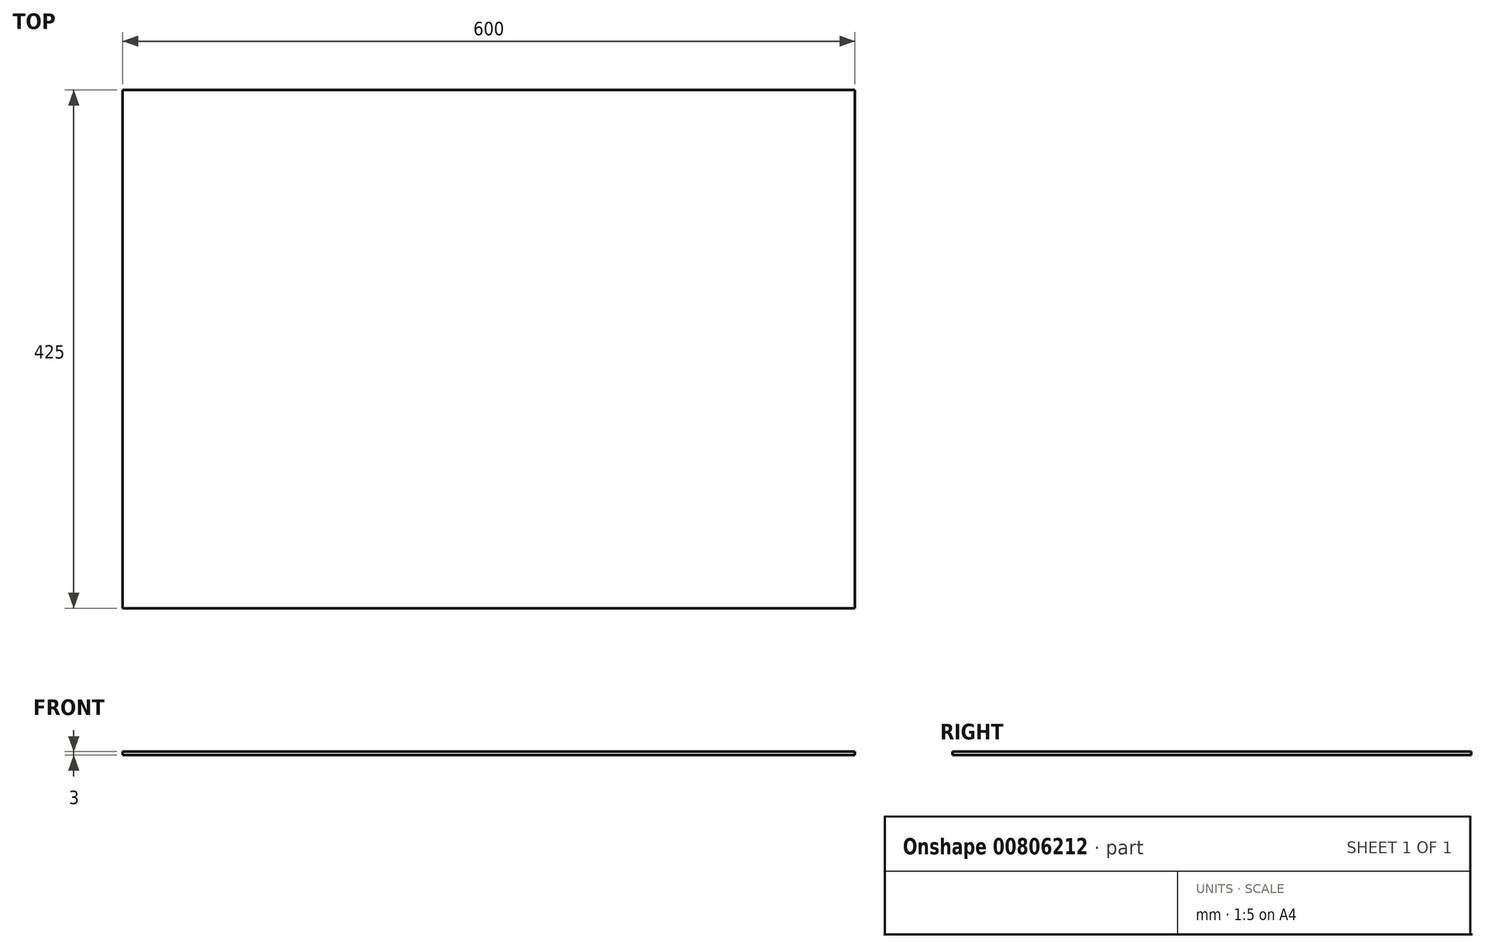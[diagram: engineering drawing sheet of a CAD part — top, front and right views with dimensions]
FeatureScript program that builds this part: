
annotation { "Feature Type Name" : "Feature", "Feature Type Description" : "" }
export const myFeature = defineFeature(function(context is Context, id is Id, definition is map)
    precondition{}
    {
        {
            var Q0;
            Q0=qCreatedBy(makeId("Top.planeOp"),FACE);
            var sketch = newSketch(context, id + "F0", { "sketchPlane" : qUnion([Q0])});
            skLineSegment(sketch, "E0.bottom", {"start": v(300, -212.5) * mm, "end": v(-300, -212.5) * mm});
            skLineSegment(sketch, "E0.top", {"start": v(300, 212.5) * mm, "end": v(-300, 212.5) * mm});
            skLineSegment(sketch, "E0.left", {"start": v(300, -212.5) * mm, "end": v(300, 212.5) * mm});
            skLineSegment(sketch, "E0.right", {"start": v(-300, -212.5) * mm, "end": v(-300, 212.5) * mm});
            skPoint(sketch, "E0.middle", {"position": v(0, 0) * mm});
            skSolve(sketch);
        }
        {
            var Q0;
            Q0=qSketchRegion(id+"F0",true);
            extrude(context, id + "F1", {"entities" : qUnion([Q0]), "depth" : 3 * mm, "offsetDistance" : 25 * mm});
        }
    });
